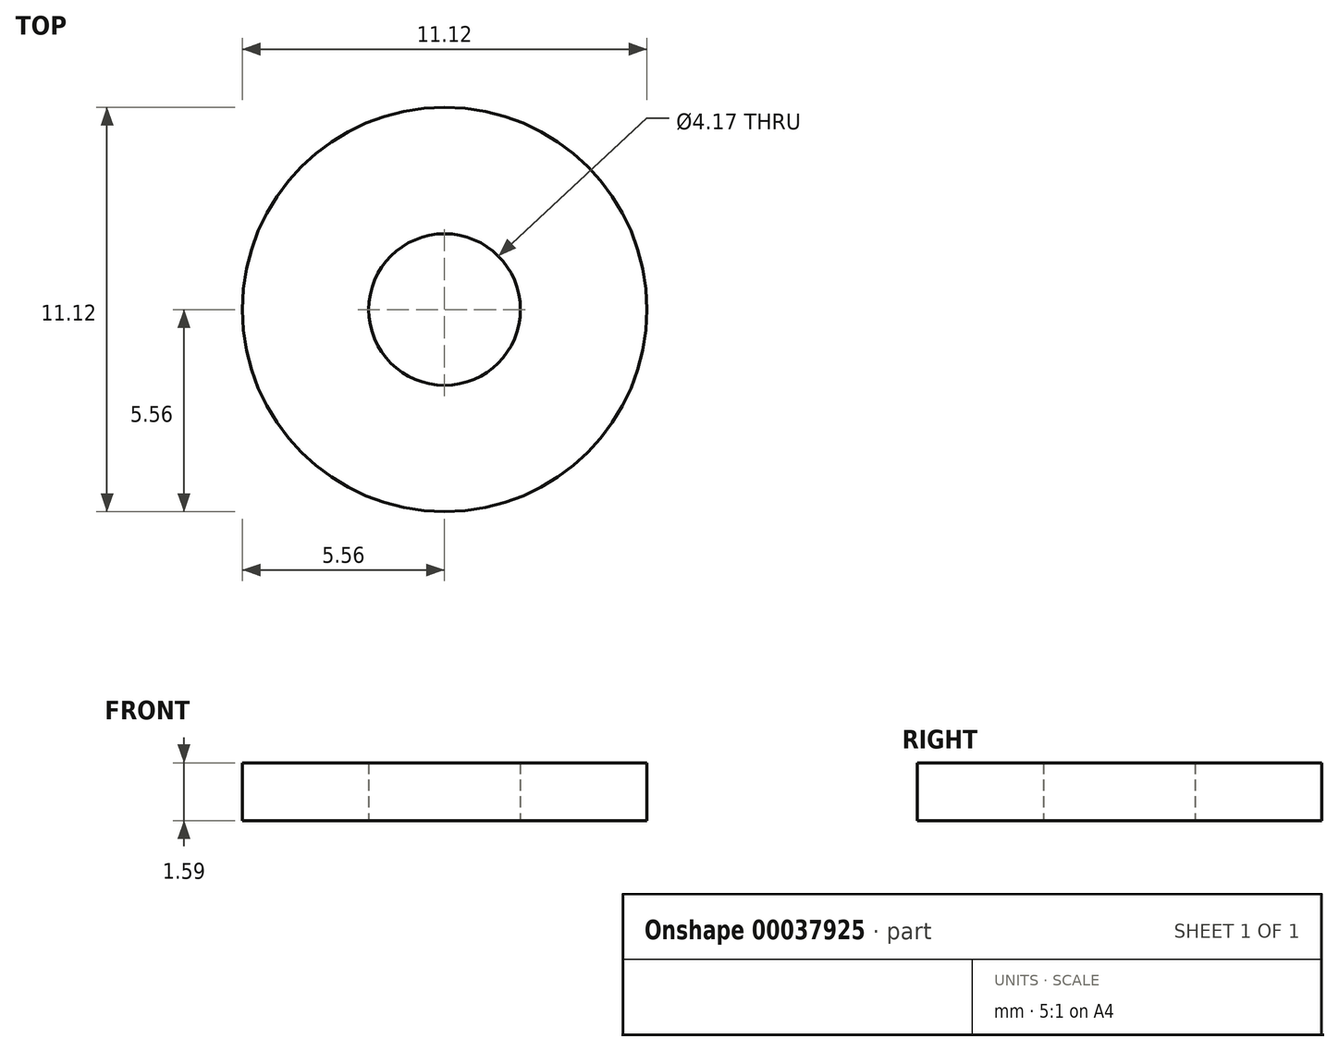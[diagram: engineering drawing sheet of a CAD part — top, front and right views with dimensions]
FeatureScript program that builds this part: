
annotation { "Feature Type Name" : "Feature", "Feature Type Description" : "" }
export const myFeature = defineFeature(function(context is Context, id is Id, definition is map)
    precondition{}
    {
        {
            var Q0;
            Q0=qCreatedBy(makeId("Top.planeOp"),FACE);
            var sketch = newSketch(context, id + "F0", { "sketchPlane" : qUnion([Q0])});
            skCircle(sketch, "E0", {"center": v(0, 0) * mm, "radius": 5.56 * mm});
            skCircle(sketch, "E1", {"center": v(0, 0) * mm, "radius": 2.08 * mm});
            skSolve(sketch);
        }
        {
            var Q0;
            Q0=qSketchRegion(id+"F0",true);
            extrude(context, id + "F1", {"entities" : qUnion([Q0]), "depth" : 1.59 * mm});
        }
    });
